# Revit family: Sanitary_Shower-Trays_Sanindusa_Versus-80-Fixed-Panel-For-Shower-Tray
name_source: partatom
category: Plumbing Fixtures
revit_build: Autodesk Revit 2018 (Build: 20170223_1515(x64)
units: mm (PartAtom-declared; Revit-internal decimal feet)

## family parameters
Always vertical = Yes
Cut with Voids When Loaded = No
OmniClass Number = 23.45.00.00
OmniClass Title = Sanitary, Laundry, and Cleaning Equipment
Part Type = Normal
Room Calculation Point = No
Round Connector Dimension = Use Diameter
Shared = No
Work Plane-Based = No

## types (1)
- Sanitary_Shower-Trays_Sanindusa_Versus-80-Fixed-Panel-For-Shower-Tray
    AssetType = Fixed
    Color = Silver
    Constituents = Aluminum profile adjustable from 0 to 20 mm; Concealed fixings, easy click cover profile and top caps; 4 mm toughened safety glass; Silicone sealants; Handle with glossy metallic finish; Fixing kit and assembly instruction.
150 mm PVC flexible hose; ABS shower bracket, with adjustable height; Fixing Kit.
    Cost = 0 $
    Description = Shower enclosure panel for shower tray
    Edition number = 1
    Element Type = SHOWER ENCLOSURES
    Features = Reversible panel, providing various application possibilities and combination; Pre-assembled, allowing for quick and easy installation; Direct installation on the floor or on the shower tray. Compatible with all Sanindusa shower trays. Easy to instal and to clean. Wide range of measures available.
For use as a grab bar and a fixed support bar for WCs, showers or washbasins. 
Generally installed parallel to a drop-down bar in a WC or on either side of a washbasin. 
Recommended if the WC pan or shower seat is a long way from the side wall. 
In the lowered position use as a grab bar, for standing up and assisting movement. For WCs or showers. Allows side access in the raised position.
Slowed down descent. Retained in upright position.
Stainless steel  for easy maintenance and hygiene.
    Finish = Bright Silver finish
    Installation Instructions = https://www.tec.sanindusa.pt
    InstallationDate = 1900-12-31T23:59:59
    Manufacturer = Sanindusa
    ManufacturerName = Sanindusa
    ManufacturerURL = www.tec.sanindusa.pt
    Material = Tempered glass, Aluminum
    ModelNumber = 8931210011
    ModelReference = Versus
    Name = Fixed panel versus 80 for shower tray
    NominalHeight = 1900 mm
    NominalLength = 800 mm
    NominalWidth = 0 mm  [stored 0 ft]
    Pre-defined type (IFC) = FURNISHING ELEMENT
    Product Guid = 719d54f9-a1c5-4f11-b4d0-afcff4bdeb78
    Product data url = https://bimobject.com
    ProductInformation = https://www.tec.sanindusa.pt
    ProductionYear = 2017
    Size = 800x1900
    Type (IFC) = IfcFurnitureType
    URL = www.tec.sanindusa.pt
    Uniclass2015Code = Pr_40_20_06_79
    Uniclass2015Title = Shower enclosures
    Uniclass2015Version = Products v1.6
    Version = 2
    WarrantyDescription = https://www.tec.sanindusa.pt
    WarrantyDurationParts = 2
    WarrantyDurationUnit = year
    WarrantyStartDate = 1900-12-31T23:59:59
1900-12-31T23:59:59
    Weight = 19.00 kg

note: [stored X ft] marks values corroborated as IEEE doubles in the binary element streams (Revit-internal decimal feet)

## geometry (parser evidence)
native form markers: Sweep x6
no freeform markers — native parametric forms only
